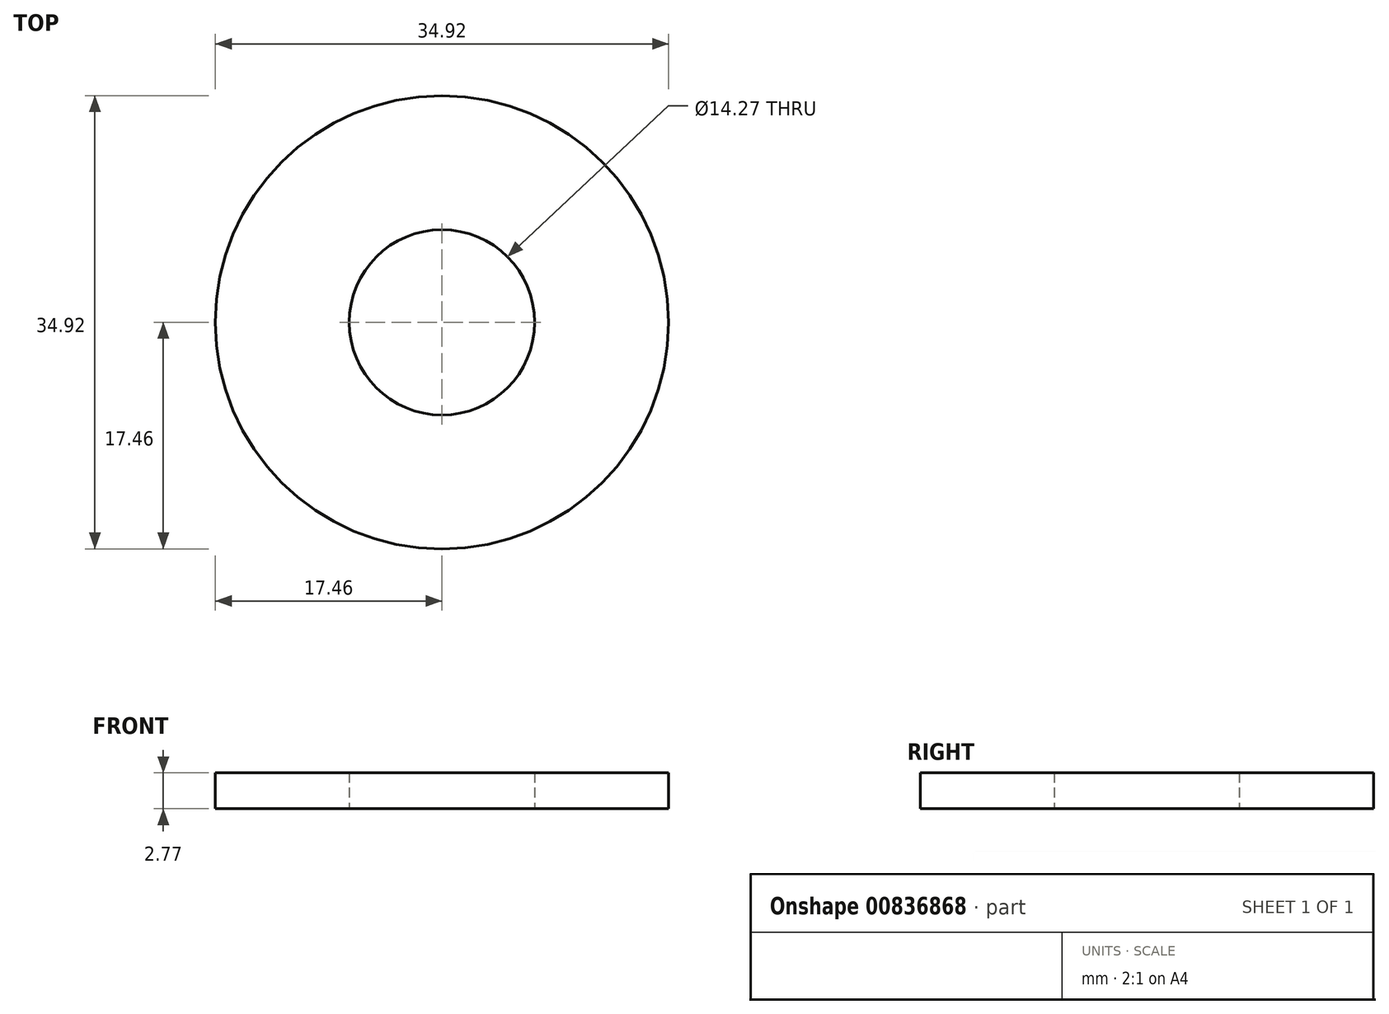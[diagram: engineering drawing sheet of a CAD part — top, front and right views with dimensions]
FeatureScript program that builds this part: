
annotation { "Feature Type Name" : "Feature", "Feature Type Description" : "" }
export const myFeature = defineFeature(function(context is Context, id is Id, definition is map)
    precondition{}
    {
        {
            var Q0;
            Q0=qCreatedBy(makeId("Top.planeOp"),FACE);
            var sketch = newSketch(context, id + "F0", { "sketchPlane" : qUnion([Q0])});
            skCircle(sketch, "E0", {"center": v(0, 0) * mm, "radius": 17.46 * mm});
            skCircle(sketch, "E1", {"center": v(0, 0) * mm, "radius": 7.14 * mm});
            skSolve(sketch);
        }
        {
            var Q0;
            Q0 = qSketchRegion(id + "F0", true);
            extrude(context, id + "F1", {"entities" : qUnion([Q0]), "depth" : 2.77 * mm, "offsetDistance" : 25.4 * mm});
        }
    });
